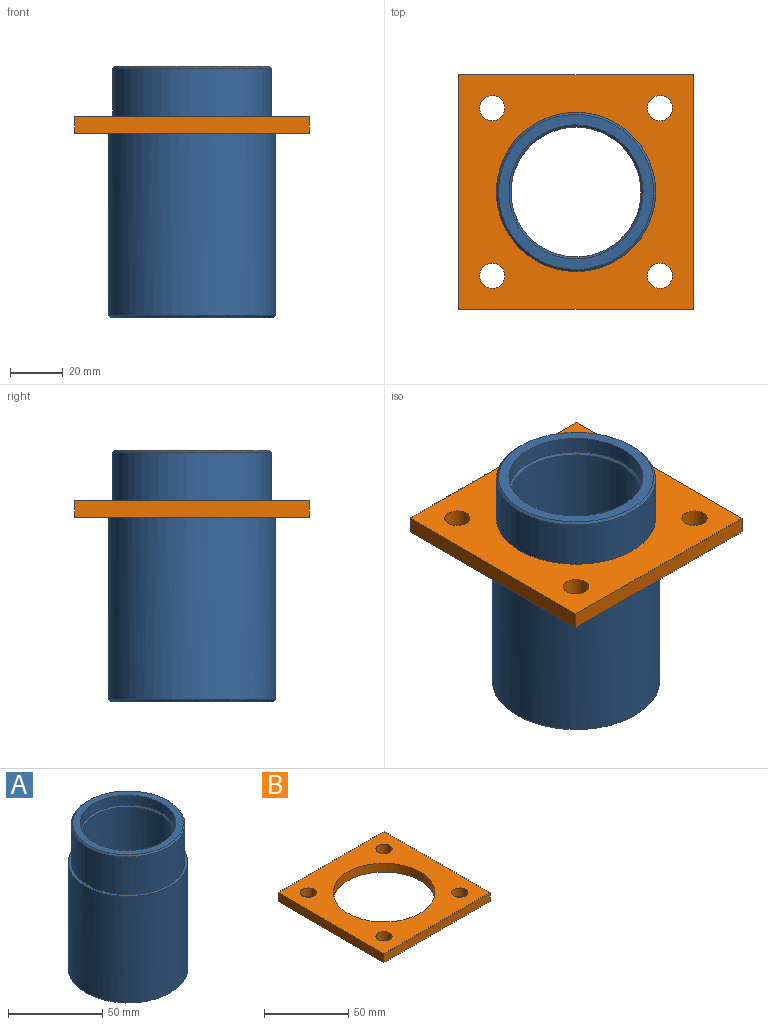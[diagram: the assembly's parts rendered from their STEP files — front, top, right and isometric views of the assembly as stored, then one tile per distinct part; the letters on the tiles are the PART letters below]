
ASSEMBLY  parts=2 mates=1
PART A: 11 faces, bbox 63.5x63.5x95.3 mm
  f0: cylinder r=24.64mm len=86.55mm, axis (0,0,1), area 13398.5mm2, adj f7,f8
  f1: cylinder r=30.16mm len=60.33mm, axis (0,0,-1), area 4657.3mm2, adj f4,f9
  f2: cylinder r=31.75mm len=69.02mm, axis (0,0,1), area 13769.8mm2, adj f4,f10
  f3: plane 61.85x61.85mm, normal (0,0,-1), area 843.7mm2, adj f8,f10
  f4: plane 63.5x63.5mm, normal (0,0,1), area 308.8mm2, adj f1,f2
  f5: plane 58.67x58.67mm, normal (0,0,1), area 677mm2, adj f6,f9
  f6: cylinder r=25.4mm len=50.8mm, axis (0,0,1), area 1013.4mm2, adj f5,f7
  f7: cone r=25.4mm half-angle=45deg, axis (0,0,1), area 169.4mm2, adj f0,f6
  f8: cone r=24.64mm half-angle=45deg, axis (0,0,-1), area 358.7mm2, adj f0,f3
  f9: cone r=29.34mm half-angle=45deg, axis (0,0,-1), area 218.2mm2, adj f1,f5
  f10: cone r=30.92mm half-angle=45deg, axis (0,0,1), area 229.9mm2, adj f2,f3
PART B: 11 faces, bbox 88.9x88.9x6.4 mm
  f0: plane 88.9x6.35mm, normal (0,-1,0), area 564.5mm2, adj f1,f8,f9,f10
  f1: plane 88.9x6.35mm, normal (1,0,0), area 564.5mm2, adj f0,f2,f9,f10
  f2: plane 88.9x6.35mm, normal (0,1,0), area 564.5mm2, adj f1,f8,f9,f10
  f3: cylinder r=30.16mm len=60.33mm, axis (0,0,1), area 1203.4mm2, adj f9,f10
  f4: cylinder r=4.76mm len=9.53mm, axis (0,0,1), area 190mm2, adj f9,f10
  f5: cylinder r=4.76mm len=9.53mm, axis (0,0,1), area 190mm2, adj f9,f10
  f6: cylinder r=4.76mm len=9.53mm, axis (0,0,1), area 190mm2, adj f9,f10
  f7: cylinder r=4.76mm len=9.53mm, axis (0,0,1), area 190mm2, adj f9,f10
  f8: plane 88.9x6.35mm, normal (-1,0,0), area 564.5mm2, adj f0,f2,f9,f10
  f9: plane 88.9x88.9mm, normal (0,0,-1), area 4760mm2, adj f0,f1,f2,f3,f4,f5,f6,f7
  f10: plane 88.9x88.9mm, normal (0,0,1), area 4760mm2, adj f0,f1,f2,f3,f4,f5,f6,f7
PLACE A at identity
PLACE B at identity fixed
MATE fastened A.f0 <-> B.f3  axis (0,0,1) through (0,0,-6.35)mm
